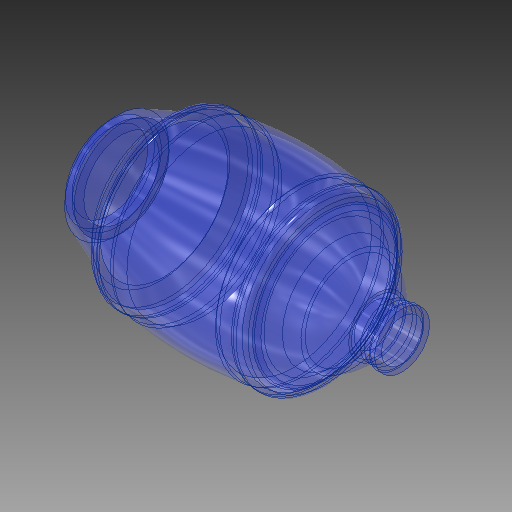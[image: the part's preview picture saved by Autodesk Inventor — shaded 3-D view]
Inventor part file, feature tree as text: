
AUTODESK INVENTOR PART (.ipt)
format: ipt  version: 2019 (Build 230136000, 136)  size: 462,336 bytes
history: native  units: mm
features: other x9, sketch x4, fillet x1
ambient origin geometry x8: Origin, YZ Plane, XZ Plane, XY Plane, X Axis, Y Axis, Z Axis, Center Point
bodies: Body1 (feature_tree)
feature tree (14):
  other  "Sólido1"
  other  "Revolução1"
  other  "Revolução2"
  other  "Revolução3"
  other  "Revolução4"
  fillet  "Arredondamento1"  Radius=57.0mm
  sketch  "Esboço1"  dims[d9=57.0mm]
  sketch  "Esboço2"  dims[d11=38.0mm]
  other  "Contorno projetado1"
  other  "Contorno projetado2"
  other  "Contorno projetado3"
  other  "Contorno projetado4"
  sketch  "Esboço3"  dims[d13=76.0mm]
  sketch  "Esboço4"  dims[d14=65.0mm d15=5.0mm d16=105.0mm d17=42.0mm d18=38.0mm d19=105.0mm d22=38.0mm d23=18.0mm d24=40.0mm d25=4.0mm d26=5.0mm d27=2.0mm d28=40.0mm d29=30.0mm d30=5.0mm d31=30.0mm d32=5.0mm d33=90.0deg d34=90.0deg d35=90.0deg d36=90.0deg d37=40.0mm]
